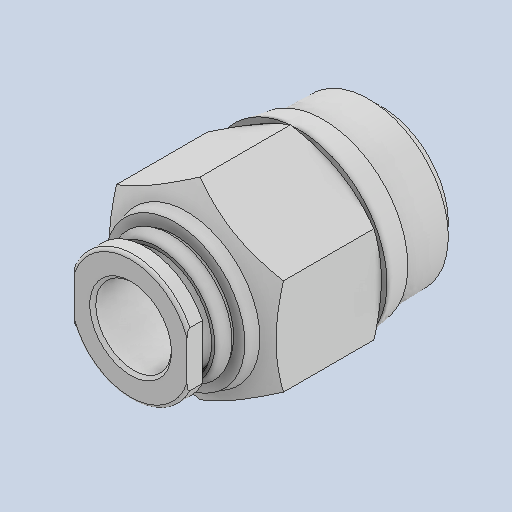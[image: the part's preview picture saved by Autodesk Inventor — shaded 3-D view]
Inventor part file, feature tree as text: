
AUTODESK INVENTOR PART (.ipt)
format: ipt  version: 2023 (Build 270158030, 158C)  size: 226,816 bytes
history: native  units: in
note: dims shown in document units (in); Inventor stores cm internally (conversion verified against a paired STEP export)
features: revolve x1, other x1
ambient origin geometry x8: Origin, YZ Plane, XZ Plane, XY Plane, X Axis, Y Axis, Z Axis, Center Point
bodies: Solid1 (feature_tree), Solid2 (feature_tree)
feature tree (2):
  revolve  "Revolve2"  [1 undecoded]
  other  "Cut-Extrude14"
note: 1 required parameter value undecoded (feature->parameter linkage not recoverable at this tier; creation-order binding heuristic only, values carry confidence <= 0.55)
